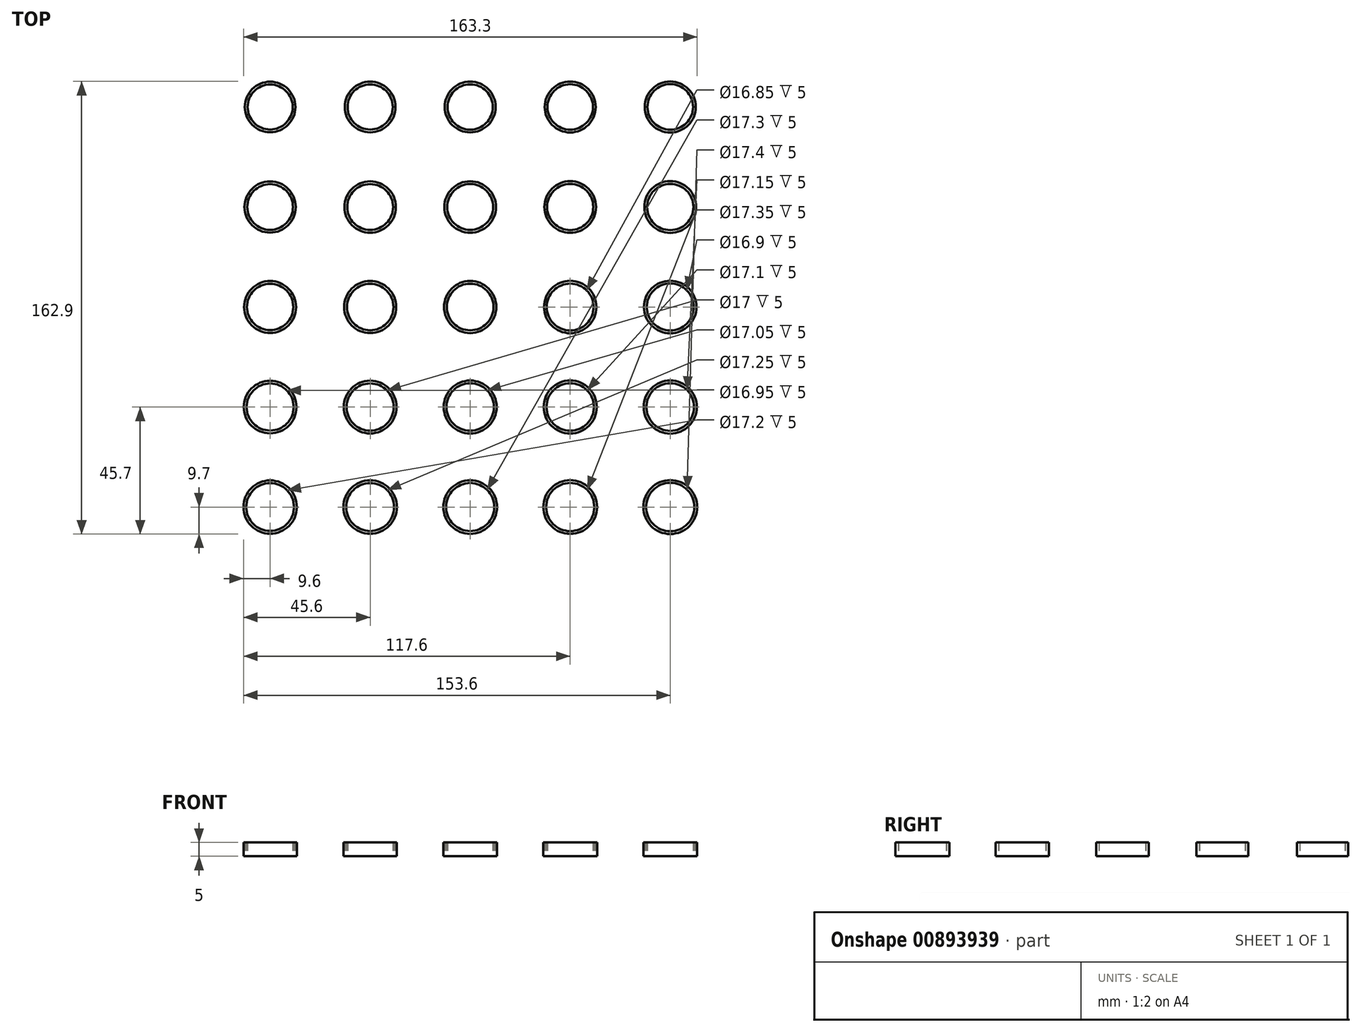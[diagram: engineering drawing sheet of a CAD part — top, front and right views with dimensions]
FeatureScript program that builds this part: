
annotation { "Feature Type Name" : "Feature", "Feature Type Description" : "" }
export const myFeature = defineFeature(function(context is Context, id is Id, definition is map)
    precondition{}
    {
        {
            var Q0;
            Q0=qCreatedBy(makeId("Top.planeOp"),FACE);
            var sketch = newSketch(context, id + "F0", { "sketchPlane" : qUnion([Q0])});
            skLineSegment(sketch, "E0.bottom", {"start": v(90, 90) * mm, "end": v(-90, 90) * mm, "construction": true});
            skLineSegment(sketch, "E0.top", {"start": v(90, -90) * mm, "end": v(-90, -90) * mm, "construction": true});
            skLineSegment(sketch, "E0.left", {"start": v(90, 90) * mm, "end": v(90, -90) * mm, "construction": true});
            skLineSegment(sketch, "E0.right", {"start": v(-90, 90) * mm, "end": v(-90, -90) * mm, "construction": true});
            skPoint(sketch, "E0.middle", {"position": v(0, 0) * mm});
            skCircle(sketch, "E1", {"center": v(0, 0) * mm, "radius": 8.4 * mm});
            skLineSegment(sketch, "E2", {"start": v(-90, 0) * mm, "end": v(90, 0) * mm, "construction": true});
            skLineSegment(sketch, "E3", {"start": v(0, 90) * mm, "end": v(0, -90) * mm, "construction": true});
            skCircle(sketch, "E4.0.1.0", {"center": v(0, 36) * mm, "radius": 8.28 * mm});
            skLineSegment(sketch, "E4.0.1.1", {"start": v(-90, 36) * mm, "end": v(90, 36) * mm, "construction": true});
            skCircle(sketch, "E4.0.2.0", {"center": v(0, 72) * mm, "radius": 8.15 * mm});
            skCircle(sketch, "E4.1.0.0", {"center": v(36, 0) * mm, "radius": 8.43 * mm});
            skCircle(sketch, "E4.1.1.0", {"center": v(36, 36) * mm, "radius": 8.3 * mm});
            skCircle(sketch, "E4.1.2.0", {"center": v(36, 72) * mm, "radius": 8.18 * mm});
            skCircle(sketch, "E4.2.0.0", {"center": v(72, 0) * mm, "radius": 8.45 * mm});
            skCircle(sketch, "E4.2.1.0", {"center": v(72, 36) * mm, "radius": 8.32 * mm});
            skCircle(sketch, "E4.2.2.0", {"center": v(72, 72) * mm, "radius": 8.2 * mm});
            skLineSegment(sketch, "E4.direction1", {"start": v(0, 0) * mm, "end": v(36, 0) * mm, "construction": true});
            skLineSegment(sketch, "E4.direction2", {"start": v(0, 0) * mm, "end": v(0, 36) * mm, "construction": true});
            skCircle(sketch, "E5.MirrorC", {"center": v(-36, 72) * mm, "radius": 8.12 * mm});
            skCircle(sketch, "E6.MirrorC", {"center": v(-36, 36) * mm, "radius": 8.25 * mm});
            skCircle(sketch, "E7.MirrorC", {"center": v(-72, 36) * mm, "radius": 8.22 * mm});
            skCircle(sketch, "E8.MirrorC", {"center": v(-72, 72) * mm, "radius": 8.1 * mm});
            skCircle(sketch, "E9.MirrorC", {"center": v(-36, 0) * mm, "radius": 8.38 * mm});
            skCircle(sketch, "E10.MirrorC", {"center": v(-72, 0) * mm, "radius": 8.35 * mm});
            skCircle(sketch, "E11.MirrorC", {"center": v(0, -36) * mm, "radius": 8.53 * mm});
            skCircle(sketch, "E12.MirrorC", {"center": v(-72, -72) * mm, "radius": 8.6 * mm});
            skCircle(sketch, "E13.MirrorC", {"center": v(-72, -36) * mm, "radius": 8.47 * mm});
            skCircle(sketch, "E14.MirrorC", {"center": v(-36, -72) * mm, "radius": 8.62 * mm});
            skCircle(sketch, "E15.MirrorC", {"center": v(-36, -36) * mm, "radius": 8.5 * mm});
            skCircle(sketch, "E16.MirrorC", {"center": v(36, -36) * mm, "radius": 8.55 * mm});
            skCircle(sketch, "E17.MirrorC", {"center": v(36, -72) * mm, "radius": 8.68 * mm});
            skCircle(sketch, "E18.MirrorC", {"center": v(72, -36) * mm, "radius": 8.57 * mm});
            skCircle(sketch, "E19.MirrorC", {"center": v(72, -72) * mm, "radius": 8.7 * mm});
            skCircle(sketch, "E20.MirrorC", {"center": v(0, -72) * mm, "radius": 8.65 * mm});
            skCircle(sketch, "E21.0", {"center": v(-72, 72) * mm, "radius": 9.1 * mm});
            skCircle(sketch, "E22.0", {"center": v(-36, 72) * mm, "radius": 9.13 * mm});
            skCircle(sketch, "E23.0", {"center": v(0, 72) * mm, "radius": 9.15 * mm});
            skCircle(sketch, "E24.0", {"center": v(36, 72) * mm, "radius": 9.18 * mm});
            skCircle(sketch, "E25.0", {"center": v(72, 72) * mm, "radius": 9.2 * mm});
            skCircle(sketch, "E26.0", {"center": v(-72, 36) * mm, "radius": 9.23 * mm});
            skCircle(sketch, "E27.0", {"center": v(-36, 36) * mm, "radius": 9.25 * mm});
            skCircle(sketch, "E28.0", {"center": v(0, 36) * mm, "radius": 9.28 * mm});
            skCircle(sketch, "E29.0", {"center": v(36, 36) * mm, "radius": 9.3 * mm});
            skCircle(sketch, "E30.0", {"center": v(72, 36) * mm, "radius": 9.32 * mm});
            skCircle(sketch, "E31.0", {"center": v(-72, 0) * mm, "radius": 9.35 * mm});
            skCircle(sketch, "E32.0", {"center": v(-36, 0) * mm, "radius": 9.38 * mm});
            skCircle(sketch, "E33.0", {"center": v(0, 0) * mm, "radius": 9.4 * mm});
            skCircle(sketch, "E34.0", {"center": v(36, 0) * mm, "radius": 9.42 * mm});
            skCircle(sketch, "E35.0", {"center": v(72, 0) * mm, "radius": 9.45 * mm});
            skCircle(sketch, "E36.0", {"center": v(-72, -36) * mm, "radius": 9.48 * mm});
            skCircle(sketch, "E37.0", {"center": v(-36, -36) * mm, "radius": 9.5 * mm});
            skCircle(sketch, "E38.0", {"center": v(0, -36) * mm, "radius": 9.53 * mm});
            skCircle(sketch, "E39.0", {"center": v(36, -36) * mm, "radius": 9.55 * mm});
            skCircle(sketch, "E40.0", {"center": v(72, -36) * mm, "radius": 9.57 * mm});
            skCircle(sketch, "E41.0", {"center": v(-72, -72) * mm, "radius": 9.6 * mm});
            skCircle(sketch, "E42.0", {"center": v(-36, -72) * mm, "radius": 9.63 * mm});
            skCircle(sketch, "E43.0", {"center": v(0, -72) * mm, "radius": 9.65 * mm});
            skCircle(sketch, "E44.0", {"center": v(36, -72) * mm, "radius": 9.67 * mm});
            skCircle(sketch, "E45.0", {"center": v(72, -72) * mm, "radius": 9.7 * mm});
            skSolve(sketch);
        }
        {
            var Q0;
            Q0=qSketchRegion(id+"F0",true);
            extrude(context, id + "F1", {"entities" : qUnion([Q0]), "depth" : 5 * mm, "offsetDistance" : 25 * mm});
        }
    });
